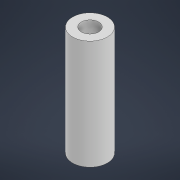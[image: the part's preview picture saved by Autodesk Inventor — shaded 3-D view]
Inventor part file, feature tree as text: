
AUTODESK INVENTOR PART (.ipt)
format: ipt  version: 2021 (Build 250183000, 183)  size: 202,752 bytes
history: native  units: mm
features: extrude x1, sketch x1
ambient origin geometry x8: Origin, YZ Plane, XZ Plane, XY Plane, X Axis, Y Axis, Z Axis, Center Point
bodies: Volumenkörper1 (feature_tree)
feature tree (2):
  extrude  "Extrusion1"  Depth=3.5mm
  sketch  "Skizze1"  dims[d0=7.0mm d1=3.5mm d2=22.0mm d3=0.0mm]
